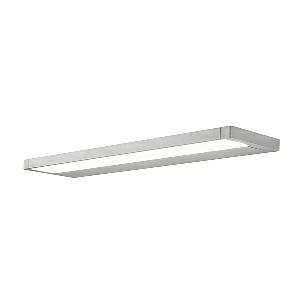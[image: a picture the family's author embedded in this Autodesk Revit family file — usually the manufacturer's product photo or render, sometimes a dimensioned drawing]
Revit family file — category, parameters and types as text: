
# Revit family: zera_bath_-_zew_3000_840_00812052_5d9f
name_source: partatom
category: Lighting Fixtures
units: mm (PartAtom-declared; Revit-internal decimal feet)

## family parameters
Cut with Voids When Loaded = No
Host = Face
Light Source = No
Part Type = Normal
Room Calculation Point = No
Round Connector Dimension = Use Diameter
Shared = No

## types (1)
- ZERA.bath - ZEW 3000/840 (1 x LED, 3300 lm, 4000K)
    Apparent Load = 27 VA
    Approval mark = CE
    CIE Flux Codes = 47 78 95 39 100
    Color Rendering = 80-89
    Color Temperature = 4000K
    Control Gear = Electronic ballast
    Default Elevation = 2000 mm  [stored 6.56168 ft]
    Description = ZEW 3000/840|Wall-mounted luminaire|light source:   Cold white   |work equipment: Power supply unit|luminous flux: 3300 lm|light distribution: Direct/indirect|class of protection: I|technology: Switchable|mains lead: Connector 2 pin|glare control: Diffusor|special features: DIN EN 60598-2-25|
    Frequency = 50 Hz, 60 Hz
    Height = 29 mm
    Lamp = 1 x LED
    Lamp Light Flux = 3300 lm
    Lamp count = 1
    Length = 600 mm
    Luminous efficacy = 122 lm/W
    Manufacturer = Waldmann
    ModVariant = No
    Model = 00812052
    Mounting Place = Wall
    Mounting Type = Surface mounted
    Number of Poles = 1
    OnlyDefault = Yes
    Power Factor = 1
    Product Name = ZERA.bath - ZEW 3000/840
    Product group = Wall mounted Luminaire
    ProductGroupID = 20
    Protection Class = Protection class I
    Protection Degree = IP 44
    RLX_Detail_Level = 1
    RLX_Emergency_Light_Flux = 0 lm
    RLX_Emergency_Type = 0
    RLX_Emergency_Type_DB = No
    RlxData = <blob elided: 35277 chars, md5=afc8da1b>
    Socket = socket
    Standby Power = 0 W
    System Light Flux = 3300 lm
    System Power = 27 W
    Type Comments = Product without accessories
    Type Image = zera_bath_20_w.jpg
    URL = http://relux.com
    VarID = ---
    Voltage = 230 V
    Voltage Range = 220-240 V
    Weight = 0.00 kg
    Width = 142 mm

note: [stored X ft] marks values corroborated as IEEE doubles in the binary element streams (Revit-internal decimal feet)

## geometry (parser evidence)
native form markers: Blend x4, Sweep x14
no freeform markers — native parametric forms only
